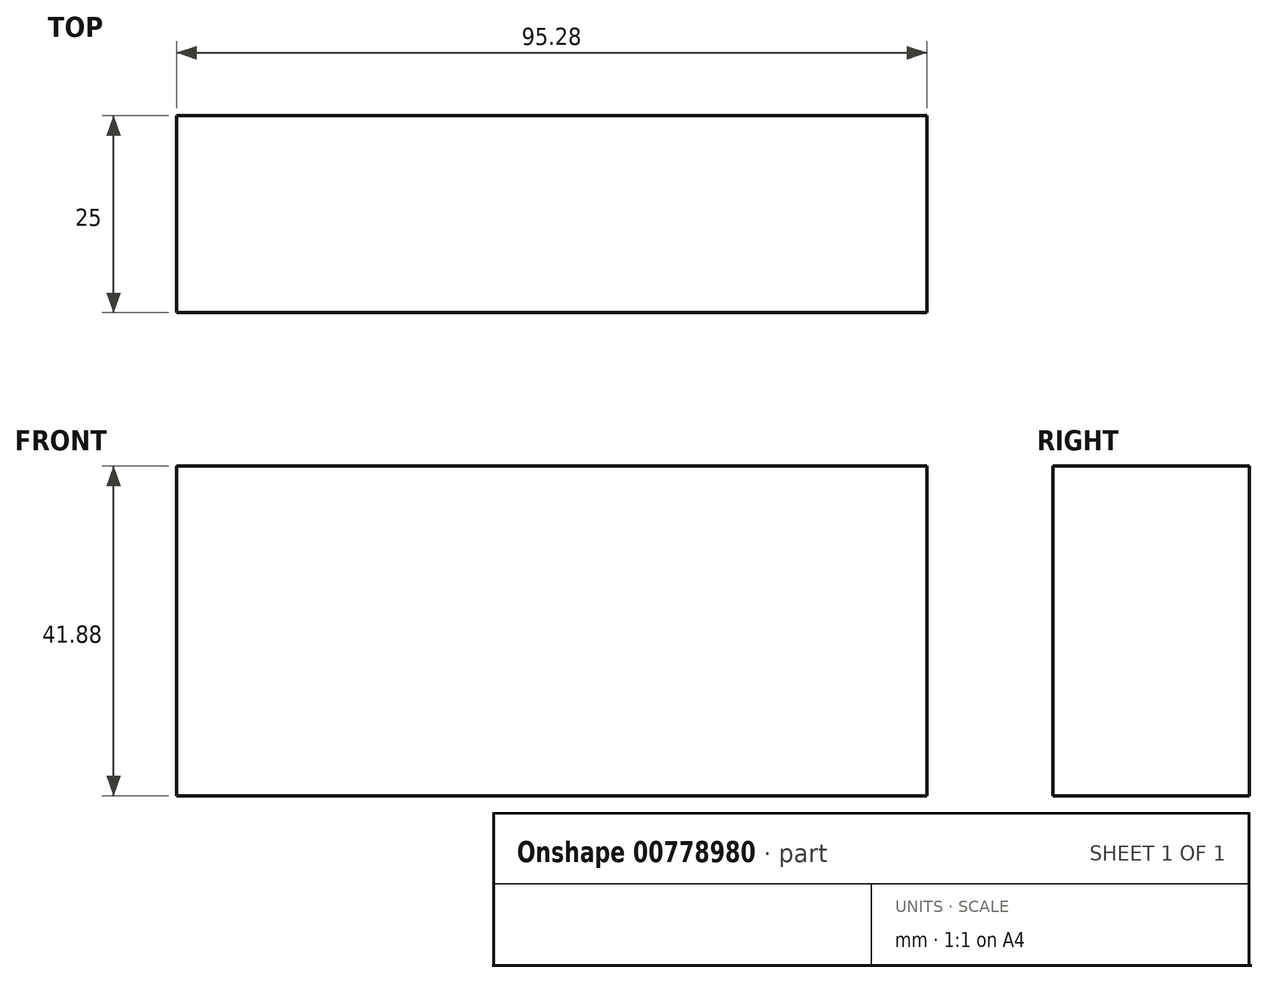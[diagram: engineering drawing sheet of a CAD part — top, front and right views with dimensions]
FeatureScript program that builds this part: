
annotation { "Feature Type Name" : "Feature", "Feature Type Description" : "" }
export const myFeature = defineFeature(function(context is Context, id is Id, definition is map)
    precondition{}
    {
        {
            var Q0;
            Q0=qCreatedBy(makeId("Front.planeOp"),FACE);
            var sketch = newSketch(context, id + "F0", { "sketchPlane" : qUnion([Q0])});
            skLineSegment(sketch, "E0.bottom", {"start": v(47.64, -20.94) * mm, "end": v(-47.64, -20.94) * mm});
            skLineSegment(sketch, "E0.top", {"start": v(47.64, 20.94) * mm, "end": v(-47.64, 20.94) * mm});
            skLineSegment(sketch, "E0.left", {"start": v(47.64, -20.94) * mm, "end": v(47.64, 20.94) * mm});
            skLineSegment(sketch, "E0.right", {"start": v(-47.64, -20.94) * mm, "end": v(-47.64, 20.94) * mm});
            skPoint(sketch, "E0.middle", {"position": v(0, 0) * mm});
            skSolve(sketch);
        }
        {
            var Q0;
            Q0 = qSketchRegion(id + "F0", true);
            extrude(context, id + "F1", {"entities" : qUnion([Q0]), "depth" : 25 * mm, "offsetDistance" : 25 * mm});
        }
    });
